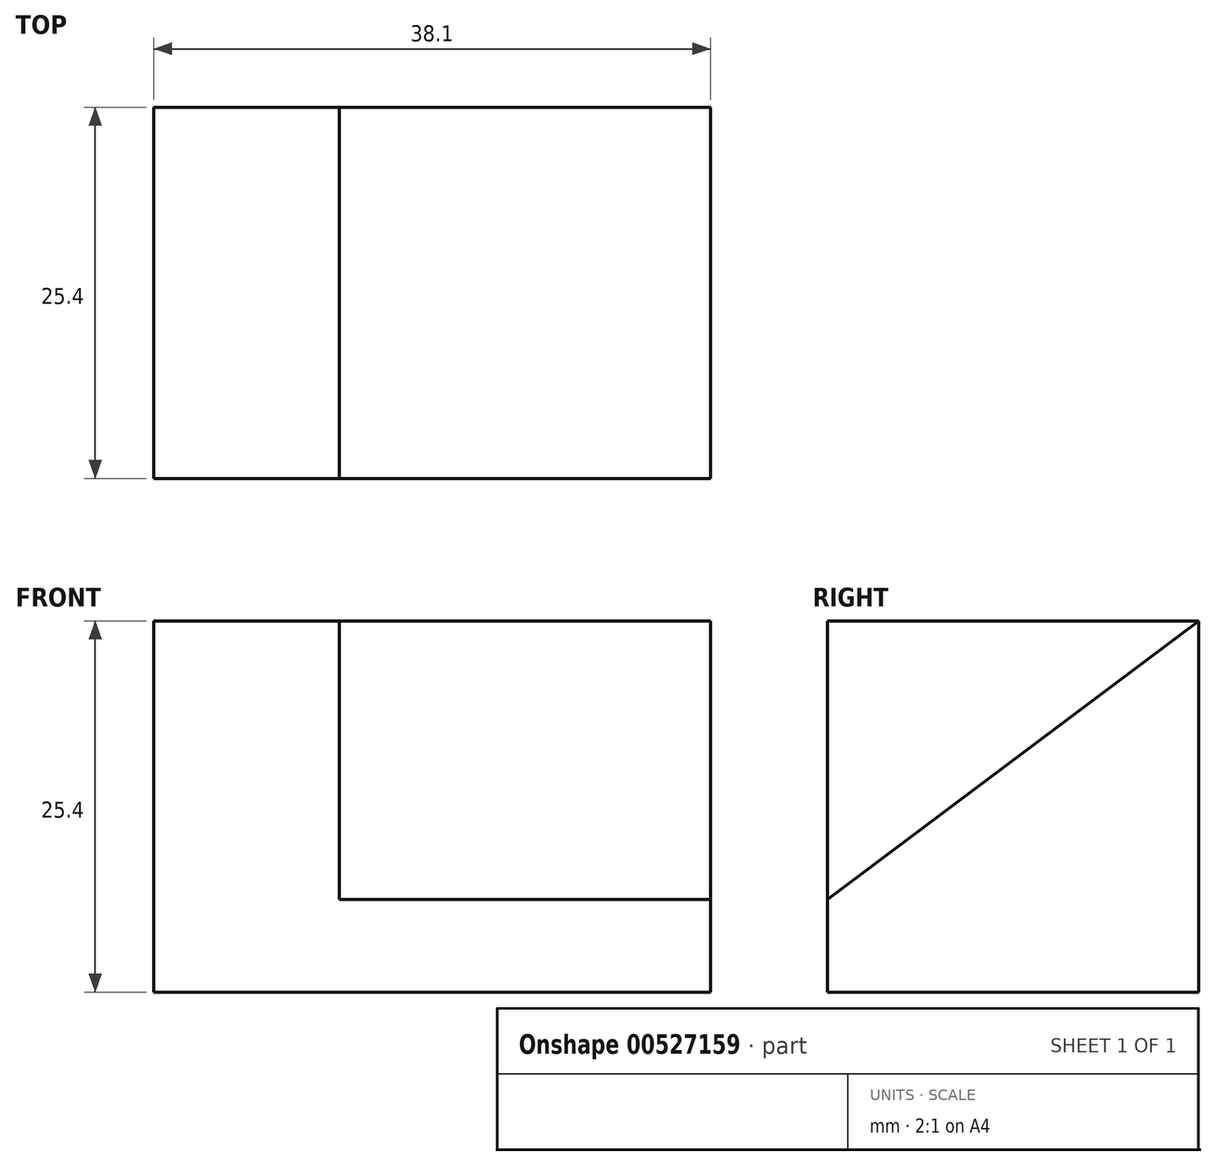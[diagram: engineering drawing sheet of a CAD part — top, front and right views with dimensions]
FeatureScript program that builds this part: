
annotation { "Feature Type Name" : "Feature", "Feature Type Description" : "" }
export const myFeature = defineFeature(function(context is Context, id is Id, definition is map)
    precondition{}
    {
        {
            var Q0;
            Q0=qCreatedBy(makeId("Right.planeOp"),FACE);
            var sketch = newSketch(context, id + "F0", { "sketchPlane" : qUnion([Q0])});
            skLineSegment(sketch, "E0", {"start": v(-25.4, 0) * mm, "end": v(-25.4, 25.4) * mm});
            skLineSegment(sketch, "E1", {"start": v(-25.4, 0) * mm, "end": v(0, 0) * mm});
            skLineSegment(sketch, "E2", {"start": v(0, 0) * mm, "end": v(0, 25.4) * mm});
            skLineSegment(sketch, "E3", {"start": v(-25.4, 25.4) * mm, "end": v(0, 25.4) * mm});
            skSolve(sketch);
        }
        {
            var Q0;
            Q0=makeQuery(id+"F0.imprint","IMPRINT",FACE,{"disambiguationData":[TD([[makeQuery(id+"F0.imprint","IMPRINT",EDGE,{"derivedFrom":sQuery(id+"F0.wireOp",EDGE,"E0")}),-1.0]])]});
            extrude(context, id + "F1", {"entities" : qUnion([Q0]), "depth" : 38.1 * mm, "offsetDistance" : 25.4 * mm});
        }
        {
            var Q0;
            Q0=makeQuery(id+"F1.opExtrude","CAP_FACE",FACE,{"disambiguationData":[OSD([sQuery(id+"F0.wireOp",EDGE,"E0"),sQuery(id+"F0.wireOp",EDGE,"E1"),sQuery(id+"F0.wireOp",EDGE,"E2"),sQuery(id+"F0.wireOp",EDGE,"E3")])],"isStart":false});
            var sketch = newSketch(context, id + "F2", { "sketchPlane" : qUnion([Q0])});
            skLineSegment(sketch, "E4", {"start": v(0, 25.4) * mm, "end": v(-25.4, 6.35) * mm});
            skSolve(sketch);
        }
        {
            var Q0;
            {var subQ0=sQuery(id+"F2.wireOp",EDGE,"E4");Q0=makeQuery(id+"F2.imprint","IMPRINT",FACE,{"disambiguationData":[TD([[makeQuery(id+"F2.imprint","IMPRINT",EDGE,{"derivedFrom":subQ0}),-1.0]])]});}
            extrude(context, id + "F3", {"entities" : qUnion([Q0]), "operationType" : NewBodyOperationType.REMOVE, "oppositeDirection" : true, "depth" : 25.4 * mm, "offsetDistance" : 25.4 * mm});
        }
    });
